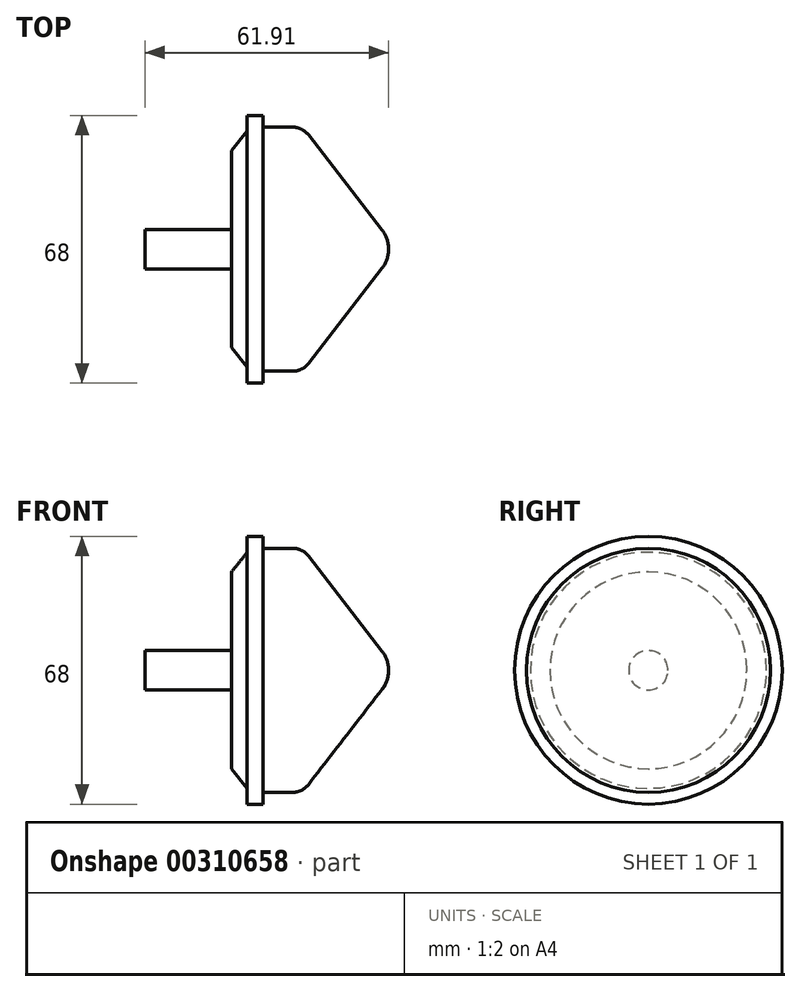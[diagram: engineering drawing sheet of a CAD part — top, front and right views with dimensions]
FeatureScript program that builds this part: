
annotation { "Feature Type Name" : "Feature", "Feature Type Description" : "" }
export const myFeature = defineFeature(function(context is Context, id is Id, definition is map)
    precondition{}
    {
        {
            var Q0;
            Q0=qCreatedBy(makeId("Front.planeOp"),FACE);
            var sketch = newSketch(context, id + "F0", { "sketchPlane" : qUnion([Q0])});
            skLineSegment(sketch, "E0", {"start": v(0, 0) * mm, "end": v(0, 25) * mm});
            skLineSegment(sketch, "E1", {"start": v(0, 0) * mm, "end": v(4, 0) * mm});
            skLineSegment(sketch, "E2", {"start": v(4, 0) * mm, "end": v(4, 30) * mm});
            skLineSegment(sketch, "E3", {"start": v(4, 30) * mm, "end": v(0, 25) * mm});
            skLineSegment(sketch, "E4", {"start": v(4, 30) * mm, "end": v(4, 34) * mm});
            skLineSegment(sketch, "E5", {"start": v(4, 34) * mm, "end": v(8, 34) * mm});
            skLineSegment(sketch, "E6", {"start": v(8, 34) * mm, "end": v(8, 0) * mm});
            skLineSegment(sketch, "E7", {"start": v(8, 0) * mm, "end": v(4, 0) * mm});
            skPoint(sketch, "E8", {"position": v(8, 31) * mm});
            skLineSegment(sketch, "E9", {"start": v(8, 31) * mm, "end": v(18, 31) * mm});
            skLineSegment(sketch, "E10", {"start": v(18, 31) * mm, "end": v(18, 0) * mm});
            skLineSegment(sketch, "E11", {"start": v(18, 0) * mm, "end": v(8, 0) * mm});
            skPoint(sketch, "E12", {"position": v(42, 0) * mm});
            skLineSegment(sketch, "E13", {"start": v(18, 31) * mm, "end": v(38.25, 4.84) * mm});
            skLineSegment(sketch, "E14", {"start": v(42, 0) * mm, "end": v(18, 0) * mm});
            skPoint(sketch, "E15", {"position": v(32, 0) * mm});
            skArc(sketch, "E16", {"start": v(39.9, 0) * mm, "mid": v(39.48, 2.56) * mm, "end": v(38.25, 4.84) * mm});
            skPoint(sketch, "E17", {"position": v(0, 5) * mm});
            skLineSegment(sketch, "E18", {"start": v(0, 5) * mm, "end": v(-22, 5) * mm});
            skLineSegment(sketch, "E19", {"start": v(-22, 5) * mm, "end": v(-22, 0) * mm});
            skLineSegment(sketch, "E20", {"start": v(-22, 0) * mm, "end": v(0, 0) * mm});
            skSolve(sketch);
        }
        {
            var Q0;
            Q0=qSketchRegion(id+"F0",true);
            var Q1;
            Q1=sQuery(id+"F0.wireOp",EDGE,"E20");
            revolve(context, id + "F1", {"entities" : qUnion([Q0]), "axis" : qUnion([Q1]), "revolveType" : RevolveType.FULL});
        }
        {
            var Q0;
            Q0=makeQuery(id+"F1.opRevolve","SWEPT_EDGE",EDGE,{"disambiguationData":[OSD([sQuery(id+"F0.wireOp",EDGE,"E9"),sQuery(id+"F0.wireOp",EDGE,"E10"),sQuery(id+"F0.wireOp",EDGE,"E13")])]});
            fillet(context, id + "F2", {"entities" : qUnion([Q0]), "radius" : 5 * mm, "tangentPropagation" : true, "allowEdgeOverflow" : false});
        }
    });
